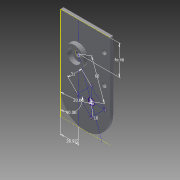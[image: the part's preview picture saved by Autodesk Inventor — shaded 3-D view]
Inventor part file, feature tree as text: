
AUTODESK INVENTOR PART (.ipt)
format: ipt  version: 2015 SP2 (Build 190223200, 223)  size: 145,408 bytes
history: native  units: mm
features: sketch x5, extrude x3, hole x3, fillet x1
ambient origin geometry x8: Origin, YZ Plane, XZ Plane, XY Plane, X Axis, Y Axis, Z Axis, Center Point
bodies: Solid1 (feature_tree)
feature tree (12):
  extrude  "Extrusion1"  Depth=80.0mm
  hole  "Hole2"  [1 undecoded]
  extrude  "Extrusion3"  Depth=40.0mm
  hole  "Hole4"  [1 undecoded]
  sketch  "Sketch8"  dims[d44=8.0mm d45=6.0mm d46=4.0mm d47=2.0mm d48=90.0deg d49=8.0mm d50=20.594885mm d53=28.972mm d56=48.0mm d57=48.0mm d58=3.490659mm d59=31.0mm d60=60.0mm d62=90.0deg d63=3.4mm d64=6.0mm d65=6.5mm d66=3.4mm d67=90.0deg d68=8.0mm d69=20.594885mm d70=10.0mm d71=7.0mm d72=0.0mm d73=40.0mm]
  hole  "Hole5"  [1 undecoded]
  extrude  "Extrusion4"  Depth=40.0mm
  fillet  "Fillet1"  Radius=31.0mm
  sketch  "Sketch1"  dims[d0=150.0mm d1=80.0mm]
  sketch  "Sketch3"  dims[d5=5.0mm d6=0.0mm]
  sketch  "Sketch6"  dims[d18=9.0mm d19=6.0mm d20=15.0mm d21=9.0mm d22=90.0deg d23=8.0mm d24=20.594885mm d38=5.0mm]
  sketch  "Sketch7"  dims[d39=7.0mm d40=0.0mm]
note: 3 required parameter values undecoded (feature->parameter linkage not recoverable at this tier; creation-order binding heuristic only, values carry confidence <= 0.55)
